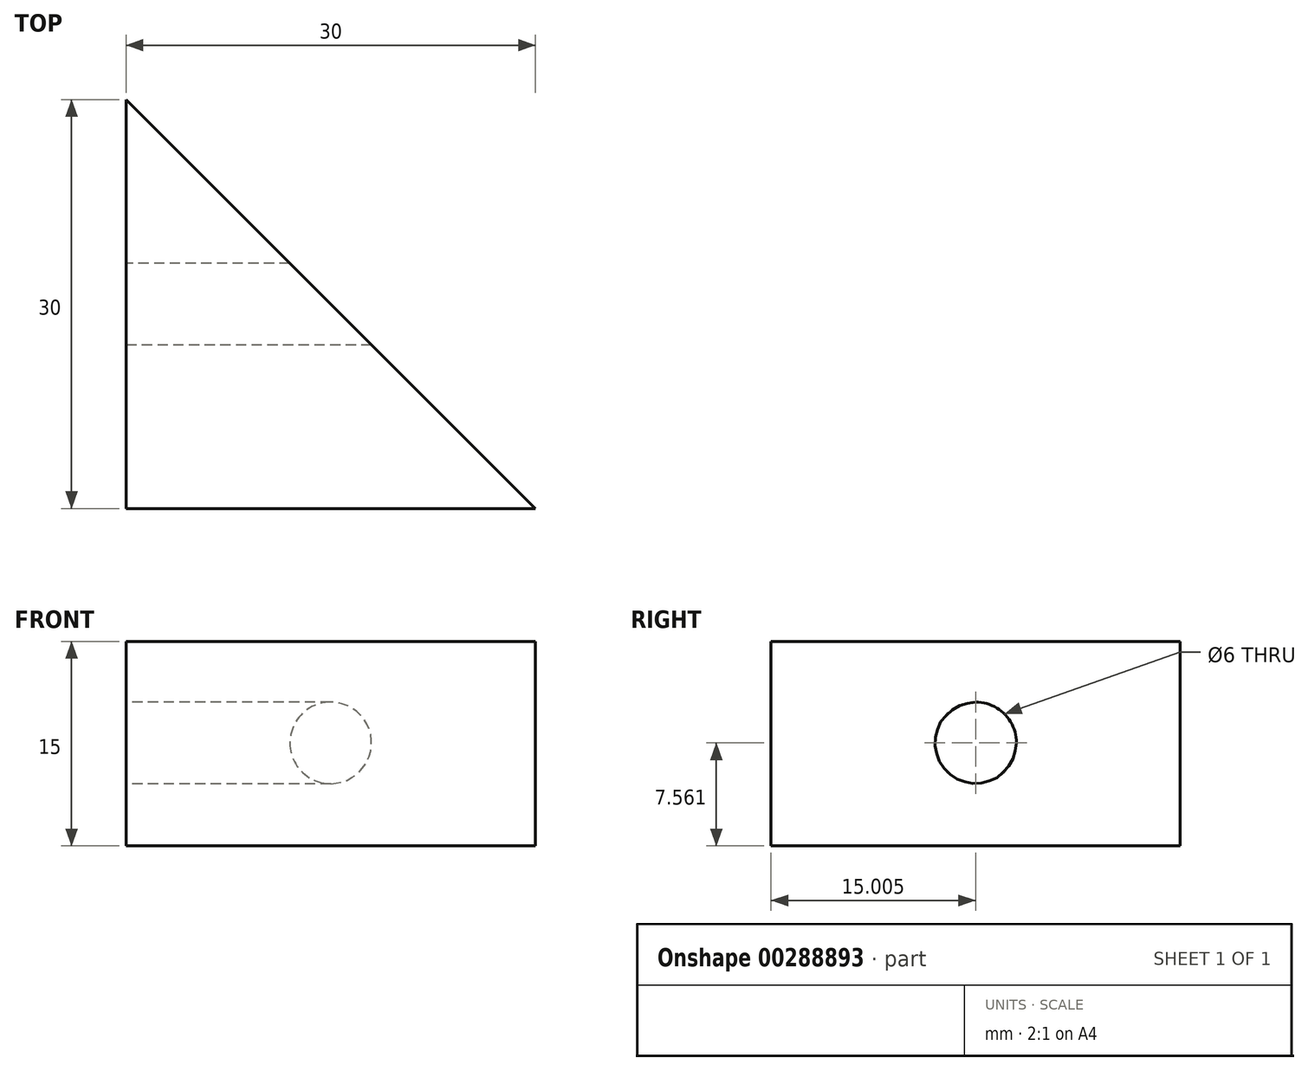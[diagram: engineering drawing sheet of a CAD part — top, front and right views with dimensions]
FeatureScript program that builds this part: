
annotation { "Feature Type Name" : "Feature", "Feature Type Description" : "" }
export const myFeature = defineFeature(function(context is Context, id is Id, definition is map)
    precondition{}
    {
        {
            var Q0;
            Q0=qCreatedBy(makeId("Top.planeOp"),FACE);
            var sketch = newSketch(context, id + "F0", { "sketchPlane" : qUnion([Q0])});
            skLineSegment(sketch, "E0", {"start": v(0, 45.26) * mm, "end": v(0, 15.26) * mm});
            skLineSegment(sketch, "E1", {"start": v(0, 15.26) * mm, "end": v(30, 15.26) * mm});
            skLineSegment(sketch, "E2", {"start": v(30, 15.26) * mm, "end": v(0, 45.26) * mm});
            skSolve(sketch);
        }
        {
            var Q0;
            Q0 = qSketchRegion(id + "F0", true);
            extrude(context, id + "F1", {"entities" : qUnion([Q0]), "depth" : 15 * mm});
        }
        {
            var Q0;
            Q0=qCreatedBy(makeId("Right.planeOp"),FACE);
            var sketch = newSketch(context, id + "F2", { "sketchPlane" : qUnion([Q0])});
            skPoint(sketch, "E3", {"position": v(30.26, 7.56) * mm});
            skLineSegment(sketch, "E4", {"start": v(30.26, 7.56) * mm, "end": v(30.26, 0) * mm, "construction": true});
            skLineSegment(sketch, "E5", {"start": v(30.26, 7.56) * mm, "end": v(30.26, 15.12) * mm, "construction": true});
            skSolve(sketch);
        }
        {
            var Q0;
            Q0=sQuery(id+"F2.wireOp",VERTEX,"E3");
            var Q1;
            Q1=makeQuery(id+"F1.opExtrude","SWEPT_BODY",BODY,{"disambiguationData":[OSD([sQuery(id+"F0.wireOp",EDGE,"E0"),sQuery(id+"F0.wireOp",EDGE,"E1"),sQuery(id+"F0.wireOp",EDGE,"E2")])]});
            hole(context, id + "F3", {"style" : HoleStyle.SIMPLE, "endStyle" : HoleEndStyle.THROUGH, "oppositeDirection" : true, "holeDiameter" : 6 * mm, "tappedDepth" : 12 * mm, "tapClearance" : 3, "locations" : qUnion([Q0]), "scope" : qUnion([Q1])});
        }
    });
